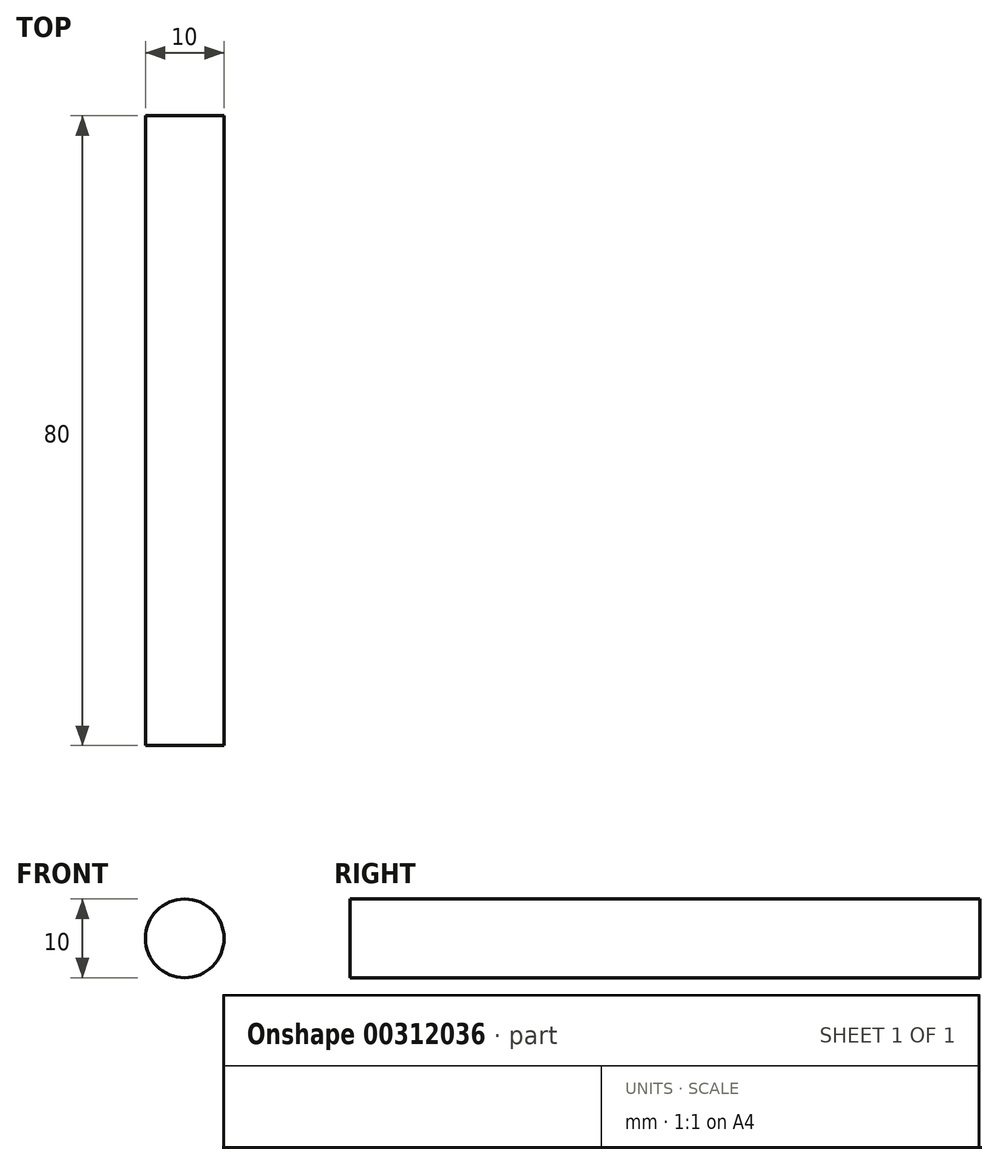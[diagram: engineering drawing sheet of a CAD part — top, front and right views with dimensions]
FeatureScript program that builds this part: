
annotation { "Feature Type Name" : "Feature", "Feature Type Description" : "" }
export const myFeature = defineFeature(function(context is Context, id is Id, definition is map)
    precondition{}
    {
        {
            var Q0;
            Q0=qCreatedBy(makeId("Front.planeOp"),FACE);
            var sketch = newSketch(context, id + "F0", { "sketchPlane" : qUnion([Q0])});
            skCircle(sketch, "E0", {"center": v(0, 0) * mm, "radius": 5 * mm});
            skSolve(sketch);
        }
        {
            var Q0;
            Q0 = qSketchRegion(id + "F0", true);
            extrude(context, id + "F1", {"entities" : qUnion([Q0]), "endBound" : BoundingType.SYMMETRIC, "depth" : 80 * mm});
        }
    });
